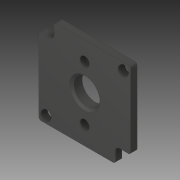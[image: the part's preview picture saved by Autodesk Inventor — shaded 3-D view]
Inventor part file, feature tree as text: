
AUTODESK INVENTOR PART (.ipt)
format: ipt  version: 2019 (Build 230136000, 136)  size: 215,040 bytes
history: native  units: in
note: dims shown in document units (in); Inventor stores cm internally (conversion verified against a paired STEP export)
features: fillet x1
ambient origin geometry x8: Origin, YZ Plane, XZ Plane, XY Plane, X Axis, Y Axis, Z Axis, Center Point
bodies: Solid1 (feature_tree)
feature tree (1):
  fillet  "Fillet4"  [1 undecoded]
note: 1 required parameter value undecoded (feature->parameter linkage not recoverable at this tier; creation-order binding heuristic only, values carry confidence <= 0.55)
